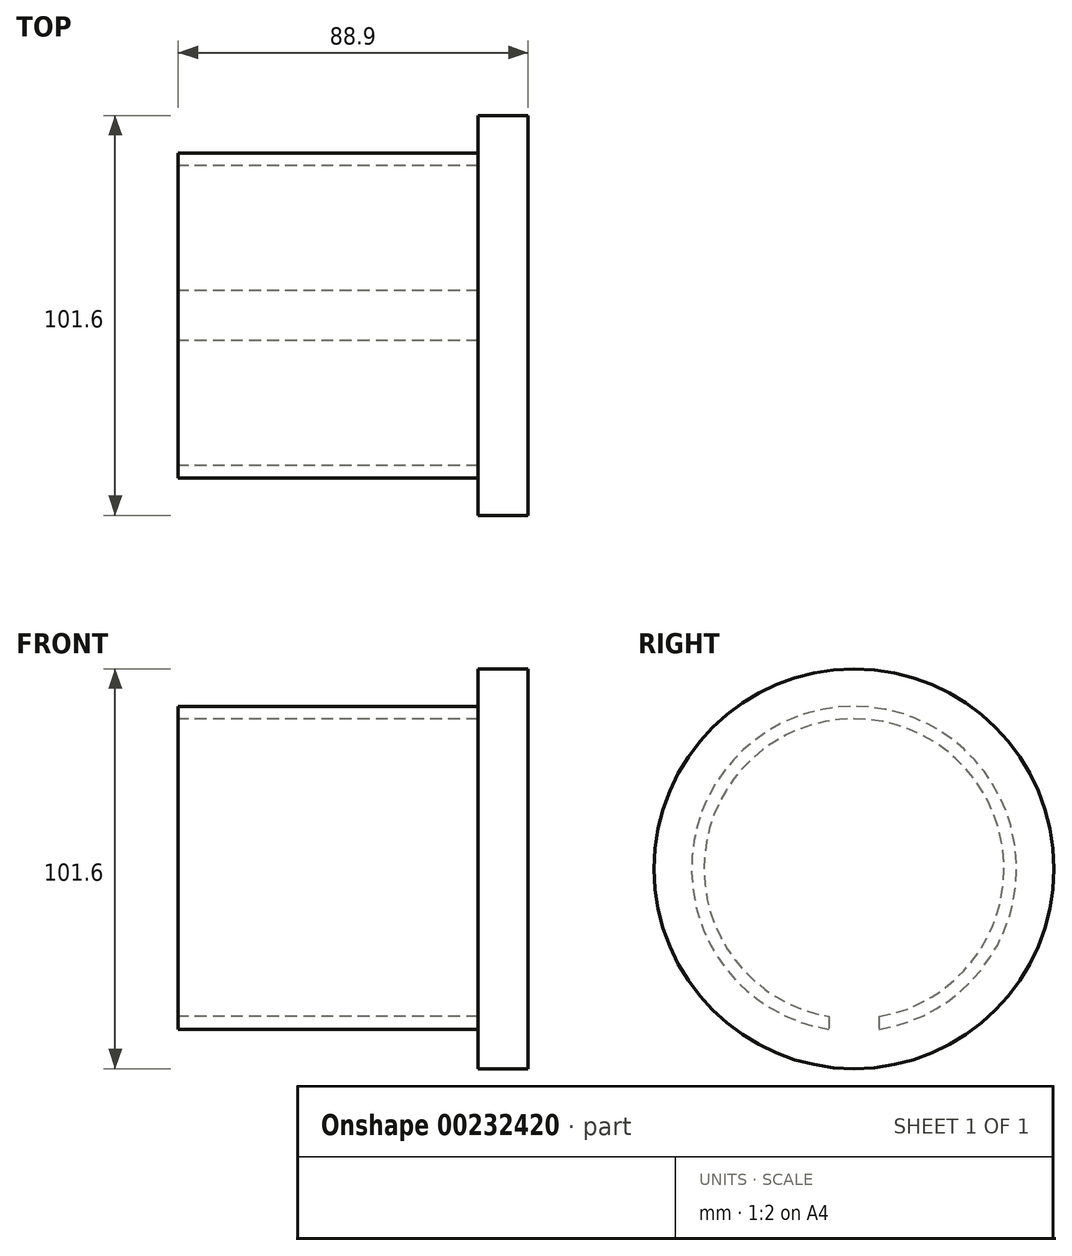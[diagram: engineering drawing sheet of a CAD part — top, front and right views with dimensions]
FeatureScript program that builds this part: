
annotation { "Feature Type Name" : "Feature", "Feature Type Description" : "" }
export const myFeature = defineFeature(function(context is Context, id is Id, definition is map)
    precondition{}
    {
        {
            var Q0;
            Q0=qCreatedBy(makeId("Right.planeOp"),FACE);
            var sketch = newSketch(context, id + "F0", { "sketchPlane" : qUnion([Q0])});
            skCircle(sketch, "E0", {"center": v(0, 0) * mm, "radius": 41.28 * mm});
            skSolve(sketch);
        }
        {
            var Q0;
            Q0=makeQuery(id+"F0.imprint","IMPRINT",FACE,{"disambiguationData":[TD([[makeQuery(id+"F0.imprint","IMPRINT",EDGE,{"derivedFrom":sQuery(id+"F0.wireOp",EDGE,"E0")}),1.0]])]});
            extrude(context, id + "F1", {"entities" : qUnion([Q0]), "depth" : 88.9 * mm});
        }
        {
            var Q0;
            Q0=makeQuery(id+"F1.opExtrude","CAP_FACE",FACE,{"disambiguationData":[OSD([sQuery(id+"F0.wireOp",EDGE,"E0")])],"isStart":false});
            var sketch = newSketch(context, id + "F2", { "sketchPlane" : qUnion([Q0])});
            skCircle(sketch, "E1", {"center": v(0, 0) * mm, "radius": 50.8 * mm});
            skSolve(sketch);
        }
        {
            var Q0;
            Q0=makeQuery(id+"F2.imprint","IMPRINT",FACE,{"disambiguationData":[TD([[makeQuery(id+"F2.imprint","IMPRINT",EDGE,{"derivedFrom":sQuery(id+"F2.wireOp",EDGE,"E1")}),1.0]])]});
            extrude(context, id + "F3", {"entities" : qUnion([Q0]), "operationType" : NewBodyOperationType.ADD, "oppositeDirection" : true, "depth" : 12.7 * mm});
        }
        {
            var Q0;
            Q0=makeQuery(id+"F0.imprint","IMPRINT",FACE,{"disambiguationData":[TD([[makeQuery(id+"F0.imprint","IMPRINT",EDGE,{"derivedFrom":sQuery(id+"F0.wireOp",EDGE,"E0")}),1.0]])]});
            var sketch = newSketch(context, id + "F4", { "sketchPlane" : qUnion([Q0])});
            skLineSegment(sketch, "E2.bottom", {"start": v(-6.35, -21.5) * mm, "end": v(6.35, -21.5) * mm});
            skLineSegment(sketch, "E2.top", {"start": v(-6.35, -97.7) * mm, "end": v(6.35, -97.7) * mm});
            skLineSegment(sketch, "E2.left", {"start": v(-6.35, -21.5) * mm, "end": v(-6.35, -97.7) * mm});
            skLineSegment(sketch, "E2.right", {"start": v(6.35, -21.5) * mm, "end": v(6.35, -97.7) * mm});
            skPoint(sketch, "E2.middle", {"position": v(0, -59.6) * mm});
            skSolve(sketch);
        }
        {
            var Q0;
            {var subQ0=sQuery(id+"F4.wireOp",EDGE,"E2.bottom");Q0=makeQuery(id+"F4.imprint","IMPRINT",FACE,{"disambiguationData":[TD([[makeQuery(id+"F4.imprint","IMPRINT",EDGE,{"derivedFrom":subQ0}),-1.0]])]});}
            extrude(context, id + "F5", {"entities" : qUnion([Q0]), "operationType" : NewBodyOperationType.REMOVE, "depth" : 76.2 * mm});
        }
        {
            var Q0;
            Q0=makeQuery(id+"F0.imprint","IMPRINT",FACE,{"disambiguationData":[TD([[makeQuery(id+"F0.imprint","IMPRINT",EDGE,{"derivedFrom":sQuery(id+"F0.wireOp",EDGE,"E0")}),1.0]])]});
            var sketch = newSketch(context, id + "F6", { "sketchPlane" : qUnion([Q0])});
            skCircle(sketch, "E3", {"center": v(0, 0) * mm, "radius": 38.1 * mm});
            skSolve(sketch);
        }
        {
            var Q0;
            Q0=makeQuery(id+"F6.imprint","IMPRINT",FACE,{"disambiguationData":[TD([[makeQuery(id+"F6.imprint","IMPRINT",EDGE,{"derivedFrom":sQuery(id+"F6.wireOp",EDGE,"E3")}),1.0]])]});
            extrude(context, id + "F7", {"entities" : qUnion([Q0]), "operationType" : NewBodyOperationType.REMOVE, "depth" : 76.2 * mm});
        }
    });
